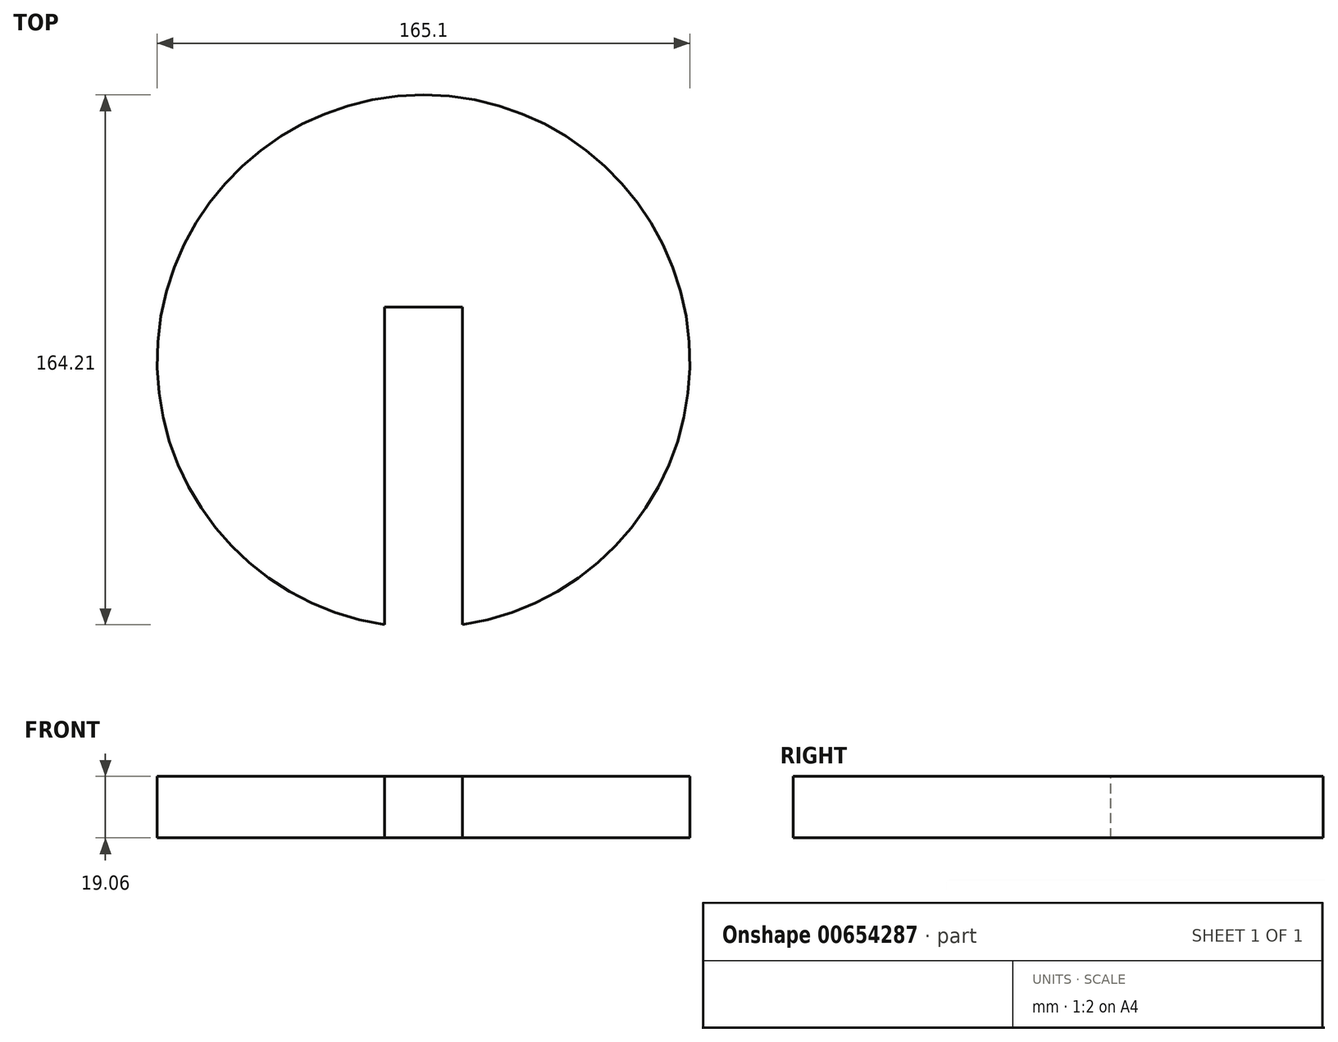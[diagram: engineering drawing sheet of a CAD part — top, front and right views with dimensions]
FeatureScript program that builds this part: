
annotation { "Feature Type Name" : "Feature", "Feature Type Description" : "" }
export const myFeature = defineFeature(function(context is Context, id is Id, definition is map)
    precondition{}
    {
        {
            var Q0;
            Q0=qCreatedBy(makeId("Top.planeOp"),FACE);
            var sketch = newSketch(context, id + "F0", { "sketchPlane" : qUnion([Q0])});
            skCircle(sketch, "E0", {"center": v(0, 0) * mm, "radius": 82.55 * mm});
            skSolve(sketch);
        }
        {
            var Q0;
            Q0=qSketchRegion(id+"F0",true);
            extrude(context, id + "F1", {"entities" : qUnion([Q0]), "endBound" : BoundingType.SYMMETRIC, "depth" : 19.05 * mm, "offsetDistance" : 25.4 * mm});
        }
        {
            var Q0;
            Q0=qCreatedBy(makeId("Top.planeOp"),FACE);
            var sketch = newSketch(context, id + "F2", { "sketchPlane" : qUnion([Q0])});
            skLineSegment(sketch, "E1.top", {"start": v(12.07, -82.62) * mm, "end": v(-12.06, -82.62) * mm});
            skPoint(sketch, "E1.middle", {"position": v(0, 0) * mm});
            skLineSegment(sketch, "E2", {"start": v(-12.06, 16.82) * mm, "end": v(12.07, 16.82) * mm});
            skLineSegment(sketch, "E3", {"start": v(-12.06, 16.82) * mm, "end": v(-12.06, -82.62) * mm});
            skLineSegment(sketch, "E4", {"start": v(12.07, 16.82) * mm, "end": v(12.07, -82.62) * mm});
            skSolve(sketch);
        }
        {
            var Q0;
            Q0 = qSketchRegion(id + "F2", true);
            extrude(context, id + "F3", {"entities" : qUnion([Q0]), "operationType" : NewBodyOperationType.REMOVE, "endBound" : BoundingType.SYMMETRIC, "oppositeDirection" : true, "depth" : 19.05 * mm, "offsetDistance" : 25.4 * mm});
        }
    });
